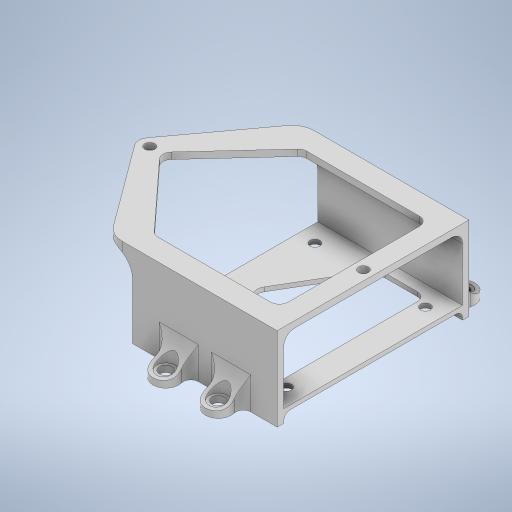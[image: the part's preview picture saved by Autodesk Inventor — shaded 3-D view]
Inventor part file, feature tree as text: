
AUTODESK INVENTOR PART (.ipt)
format: ipt  version: 2024 (Build 280153000, 153)  size: 542,208 bytes
history: native  units: in
note: dims shown in document units (in); Inventor stores cm internally (conversion verified against a paired STEP export)
features: extrude x8, fillet x7, projected_geometry x2, plane x1
ambient origin geometry x8: Origin, YZ Plane, XZ Plane, XY Plane, X Axis, Y Axis, Z Axis, Center Point
bodies: Solid1 (feature_tree)
feature tree (18):
  extrude  "Extrusion1"  Depth=3.2874in
  extrude  "Extrusion2"  Depth=0.1181in
  extrude  "Extrusion3"  Depth=0.1181in
  extrude  "Extrusion5"  Depth=0.1969in
  extrude  "Extrusion6"  Depth=0.1969in
  fillet  "Fillet1"  Radius=0.4724in
  extrude  "Extrusion7"  Depth=0.4724in
  extrude  "Extrusion8"  Depth=2.6575in
  plane  "Work Plane1"
  extrude  "Extrusion9"  Depth=1.3287in
  fillet  "Fillet2"  Radius=1.6437in
  fillet  "Fillet3"  Radius=0.0787in
  fillet  "Fillet4"  Radius=1.2598in
  fillet  "Fillet5"  Radius=0.2756in
  fillet  "Fillet6"  Radius=0.2756in
  fillet  "Fillet7"  Radius=4.3504in
  projected_geometry  "Projected Loop1"
  projected_geometry  "Projected Loop2"
